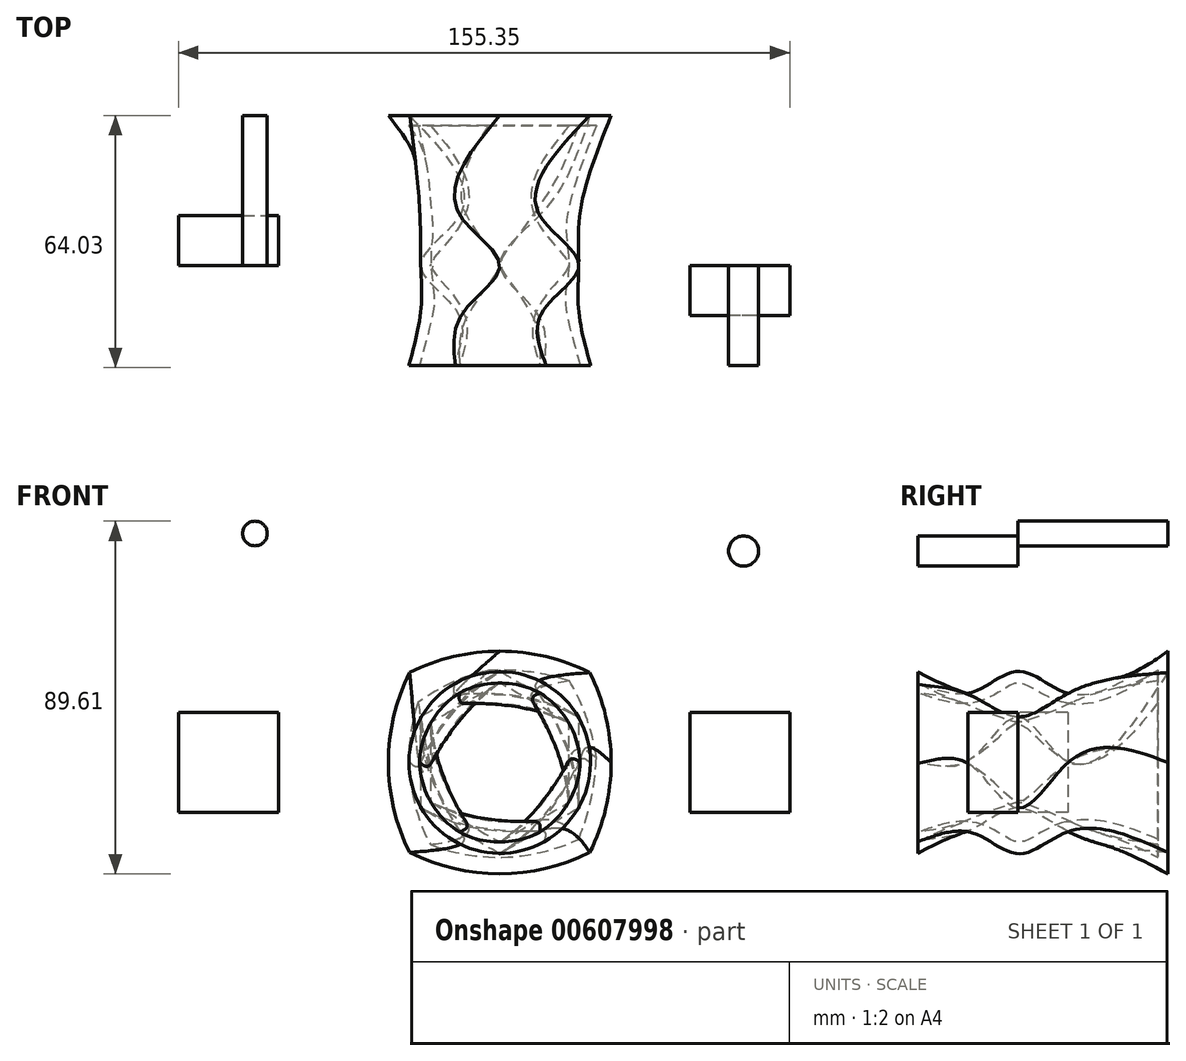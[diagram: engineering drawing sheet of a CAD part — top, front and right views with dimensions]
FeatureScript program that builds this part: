
annotation { "Feature Type Name" : "Feature", "Feature Type Description" : "" }
export const myFeature = defineFeature(function(context is Context, id is Id, definition is map)
    precondition{}
    {
        {
            var Q0;
            Q0=qCreatedBy(makeId("Front.planeOp"),FACE);
            var sketch = newSketch(context, id + "F0", { "sketchPlane" : qUnion([Q0])});
            skCircle(sketch, "E0.cCircle", {"center": v(0, 0) * mm, "radius": 20.08 * mm, "construction": true});
            skLineSegment(sketch, "E0.0", {"start": v(20.08, 11.6) * mm, "end": v(20.08, -11.6) * mm});
            skLineSegment(sketch, "E0.1", {"start": v(20.08, -11.6) * mm, "end": v(0, -23.18) * mm});
            skLineSegment(sketch, "E0.2", {"start": v(0, -23.18) * mm, "end": v(-20.08, -11.6) * mm});
            skLineSegment(sketch, "E0.3", {"start": v(-20.08, -11.6) * mm, "end": v(-20.08, 11.6) * mm});
            skLineSegment(sketch, "E0.4", {"start": v(-20.08, 11.6) * mm, "end": v(0, 23.18) * mm});
            skLineSegment(sketch, "E0.5", {"start": v(0, 23.18) * mm, "end": v(20.08, 11.6) * mm});
            skPoint(sketch, "E0.0.midPoint", {"position": v(20.08, 0) * mm});
            skSolve(sketch);
        }
        {
            var Q0;
            Q0=qCreatedBy(makeId("Front.planeOp"),FACE);
            var sketch = newSketch(context, id + "F1", { "sketchPlane" : qUnion([Q0])});
            skLineSegment(sketch, "E1.bottom", {"start": v(73.7, 12.7) * mm, "end": v(48.3, 12.7) * mm});
            skLineSegment(sketch, "E1.top", {"start": v(73.7, -12.7) * mm, "end": v(48.3, -12.7) * mm});
            skLineSegment(sketch, "E1.left", {"start": v(73.7, 12.7) * mm, "end": v(73.7, -12.7) * mm});
            skLineSegment(sketch, "E1.right", {"start": v(48.3, 12.7) * mm, "end": v(48.3, -12.7) * mm});
            skPoint(sketch, "E1.middle", {"position": v(61, 0) * mm});
            skSolve(sketch);
        }
        {
            var Q0;
            Q0 = qSketchRegion(id + "F1", true);
            extrude(context, id + "F2", {"entities" : qUnion([Q0]), "depth" : 12.7 * mm, "offsetDistance" : 25.4 * mm});
        }
        {
            var Q0;
            Q0=makeQuery(id+"F2.opExtrude","CAP_FACE",FACE,{"disambiguationData":[OSD([sQuery(id+"F1.wireOp",EDGE,"E1.bottom"),sQuery(id+"F1.wireOp",EDGE,"E1.top"),sQuery(id+"F1.wireOp",EDGE,"E1.left"),sQuery(id+"F1.wireOp",EDGE,"E1.right")])],"isStart":false});
            var sketch = newSketch(context, id + "F3", { "sketchPlane" : qUnion([Q0])});
            skCircle(sketch, "E2.cCircle", {"center": v(0, 0) * mm, "radius": 17.48 * mm, "construction": true});
            skLineSegment(sketch, "E2.0", {"start": v(20.18, -0.24) * mm, "end": v(9.88, -17.6) * mm});
            skLineSegment(sketch, "E2.1", {"start": v(9.88, -17.6) * mm, "end": v(-10.3, -17.36) * mm});
            skLineSegment(sketch, "E2.2", {"start": v(-10.3, -17.36) * mm, "end": v(-20.18, 0.24) * mm});
            skLineSegment(sketch, "E2.3", {"start": v(-20.18, 0.24) * mm, "end": v(-9.88, 17.6) * mm});
            skLineSegment(sketch, "E2.4", {"start": v(-9.88, 17.6) * mm, "end": v(10.3, 17.36) * mm});
            skLineSegment(sketch, "E2.5", {"start": v(10.3, 17.36) * mm, "end": v(20.18, -0.24) * mm});
            skPoint(sketch, "E2.0.midPoint", {"position": v(15.03, -8.92) * mm});
            skSolve(sketch);
        }
        {
            var Q0;
            Q0=qCreatedBy(makeId("Front.planeOp"),FACE);
            var sketch = newSketch(context, id + "F4", { "sketchPlane" : qUnion([Q0])});
            skLineSegment(sketch, "E3.bottom", {"start": v(-81.65, 12.7) * mm, "end": v(-56.25, 12.7) * mm});
            skLineSegment(sketch, "E3.top", {"start": v(-81.65, -12.7) * mm, "end": v(-56.25, -12.7) * mm});
            skLineSegment(sketch, "E3.left", {"start": v(-81.65, 12.7) * mm, "end": v(-81.65, -12.7) * mm});
            skLineSegment(sketch, "E3.right", {"start": v(-56.25, 12.7) * mm, "end": v(-56.25, -12.7) * mm});
            skPoint(sketch, "E3.middle", {"position": v(-68.95, 0) * mm});
            skSolve(sketch);
        }
        {
            var Q0;
            Q0 = qSketchRegion(id + "F4", true);
            extrude(context, id + "F5", {"entities" : qUnion([Q0]), "oppositeDirection" : true, "depth" : 12.7 * mm, "offsetDistance" : 25.4 * mm});
        }
        {
            var Q0;
            Q0=makeQuery(id+"F5.opExtrude","CAP_FACE",FACE,{"disambiguationData":[OSD([sQuery(id+"F4.wireOp",EDGE,"E3.bottom"),sQuery(id+"F4.wireOp",EDGE,"E3.top"),sQuery(id+"F4.wireOp",EDGE,"E3.left"),sQuery(id+"F4.wireOp",EDGE,"E3.right")])],"isStart":false});
            var sketch = newSketch(context, id + "F6", { "sketchPlane" : qUnion([Q0])});
            skCircle(sketch, "E4.cCircle", {"center": v(0, 0) * mm, "radius": 17.56 * mm, "construction": true});
            skLineSegment(sketch, "E4.0", {"start": v(20.28, 0.07) * mm, "end": v(10.2, -17.53) * mm});
            skLineSegment(sketch, "E4.1", {"start": v(10.2, -17.53) * mm, "end": v(-10.08, -17.6) * mm});
            skLineSegment(sketch, "E4.2", {"start": v(-10.08, -17.6) * mm, "end": v(-20.28, -0.07) * mm});
            skLineSegment(sketch, "E4.3", {"start": v(-20.28, -0.07) * mm, "end": v(-10.2, 17.53) * mm});
            skLineSegment(sketch, "E4.4", {"start": v(-10.2, 17.53) * mm, "end": v(10.08, 17.6) * mm});
            skLineSegment(sketch, "E4.5", {"start": v(10.08, 17.6) * mm, "end": v(20.28, 0.07) * mm});
            skPoint(sketch, "E4.0.midPoint", {"position": v(15.24, -8.73) * mm});
            skSolve(sketch);
        }
        {
            var Q0;
            Q0=qCreatedBy(makeId("Front.planeOp"),FACE);
            var sketch = newSketch(context, id + "F7", { "sketchPlane" : qUnion([Q0])});
            skCircle(sketch, "E5", {"center": v(61.96, 53.73) * mm, "radius": 3.83 * mm});
            skSolve(sketch);
        }
        {
            var Q0;
            Q0 = qSketchRegion(id + "F7", true);
            extrude(context, id + "F8", {"entities" : qUnion([Q0]), "depth" : 25.4 * mm, "offsetDistance" : 25.4 * mm});
        }
        {
            var Q0;
            Q0=makeQuery(id+"F8.opExtrude","CAP_FACE",FACE,{"disambiguationData":[OSD([sQuery(id+"F7.wireOp",EDGE,"E5")])],"isStart":false});
            var sketch = newSketch(context, id + "F9", { "sketchPlane" : qUnion([Q0])});
            skCircle(sketch, "E6", {"center": v(0, 0) * mm, "radius": 23.06 * mm});
            skSolve(sketch);
        }
        {
            var Q0;
            Q0=qCreatedBy(makeId("Front.planeOp"),FACE);
            var sketch = newSketch(context, id + "F10", { "sketchPlane" : qUnion([Q0])});
            skCircle(sketch, "E7", {"center": v(-62.18, 58.19) * mm, "radius": 3.13 * mm});
            skSolve(sketch);
        }
        {
            var Q0;
            Q0 = qSketchRegion(id + "F10", true);
            extrude(context, id + "F11", {"entities" : qUnion([Q0]), "oppositeDirection" : true, "depth" : 38.1 * mm, "offsetDistance" : 25.4 * mm});
        }
        {
            var Q0;
            Q0=makeQuery(id+"F11.opExtrude","CAP_FACE",FACE,{"disambiguationData":[OSD([sQuery(id+"F10.wireOp",EDGE,"E7")])],"isStart":false});
            var sketch = newSketch(context, id + "F12", { "sketchPlane" : qUnion([Q0])});
            skPoint(sketch, "E8.middle", {"position": v(0, 0) * mm});
            skPoint(sketch, "E8.right.start.orphan", {"position": v(-22.86, 22.86) * mm});
            skPoint(sketch, "E9", {"position": v(-22.86, -22.86) * mm});
            skPoint(sketch, "E10", {"position": v(22.86, -22.86) * mm});
            skPoint(sketch, "E11", {"position": v(22.86, 22.86) * mm});
            skArc(sketch, "E12", {"start": v(-22.86, 22.86) * mm, "mid": v(-28.3, 0) * mm, "end": v(-22.86, -22.86) * mm});
            skArc(sketch, "E13", {"start": v(22.86, 22.86) * mm, "mid": v(0, 28.3) * mm, "end": v(-22.86, 22.86) * mm});
            skArc(sketch, "E14", {"start": v(22.86, -22.86) * mm, "mid": v(28.3, 0) * mm, "end": v(22.86, 22.86) * mm});
            skArc(sketch, "E15", {"start": v(-22.86, -22.86) * mm, "mid": v(0, -28.3) * mm, "end": v(22.86, -22.86) * mm});
            skSolve(sketch);
        }
        {
            var Q0;
            Q0=makeQuery(id+"F12.imprint","IMPRINT",FACE,{"disambiguationData":[TD([[makeQuery(id+"F12.imprint","IMPRINT",EDGE,{"derivedFrom":sQuery(id+"F12.wireOp",EDGE,"E12")}),1.0]])]});
            var Q1;
            Q1=makeQuery(id+"F6.imprint","IMPRINT",FACE,{"disambiguationData":[TD([[makeQuery(id+"F6.imprint","IMPRINT",EDGE,{"derivedFrom":sQuery(id+"F6.wireOp",EDGE,"E4.0")}),-1.0]])]});
            var Q2;
            Q2=makeQuery(id+"F0.imprint","IMPRINT",FACE,{"disambiguationData":[TD([[makeQuery(id+"F0.imprint","IMPRINT",EDGE,{"derivedFrom":sQuery(id+"F0.wireOp",EDGE,"E0.0")}),-1.0]])]});
            var Q3;
            Q3=makeQuery(id+"F3.imprint","IMPRINT",FACE,{"disambiguationData":[TD([[makeQuery(id+"F3.imprint","IMPRINT",EDGE,{"derivedFrom":sQuery(id+"F3.wireOp",EDGE,"E2.0")}),-1.0]])]});
            var Q4;
            Q4=makeQuery(id+"F9.imprint","IMPRINT",FACE,{"disambiguationData":[TD([[makeQuery(id+"F9.imprint","IMPRINT",EDGE,{"derivedFrom":sQuery(id+"F9.wireOp",EDGE,"E6")}),1.0]])]});
            loft(context, id + "F13", {"sheetProfilesArray" : [{ "sheetProfileEntities" : qUnion([Q0]) }, { "sheetProfileEntities" : qUnion([Q1]) }, { "sheetProfileEntities" : qUnion([Q2]) }, { "sheetProfileEntities" : qUnion([Q3]) }, { "sheetProfileEntities" : qUnion([Q4]) }]});
        }
        {
            var Q0;
            Q0=makeQuery(id+"F13.opLoft","CAP_FACE",FACE,{"disambiguationData":[OSD([makeQuery(id+"F9.imprint","IMPRINT",FACE,{"disambiguationData":[TD([[makeQuery(id+"F9.imprint","IMPRINT",EDGE,{"derivedFrom":sQuery(id+"F9.wireOp",EDGE,"E6")}),1.0]])]})])],"isStart":true});
            shell(context, id + "F14", {"entities" : qUnion([Q0]), "thickness" : 2.54 * mm});
        }
    });
